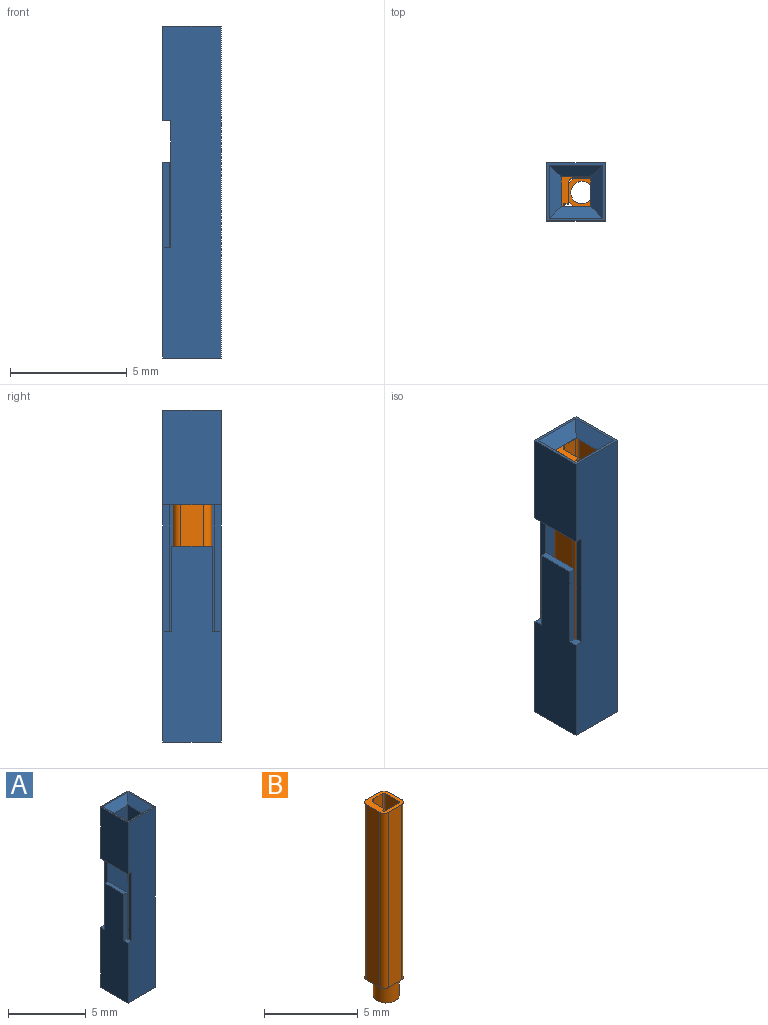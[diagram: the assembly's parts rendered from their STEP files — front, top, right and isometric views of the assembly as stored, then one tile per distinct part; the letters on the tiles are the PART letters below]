
ASSEMBLY  parts=2 mates=1
PART A: 25 faces, bbox 2.5x2.5x14.2 mm
  f0: plane 14.22x2.49mm, normal (0,-1,0), area 33.6mm2, adj f1,f2,f7,f12,f14,f20,f22,f23
  f1: plane 8.38x2.49mm, normal (-1,0,0), area 18.1mm2, adj f0,f7,f13,f17,f18,f19,f20,f21
  f2: plane 4.06x2.49mm, normal (-1,0,0), area 10.1mm2, adj f0,f13,f14,f22
  f3: plane 13.72x1.91mm, normal (0,1,0), area 25.9mm2, adj f4,f5,f7,f15,f16,f20,f22,f23
  f4: plane 8.38x1.91mm, normal (1,0,0), area 15.3mm2, adj f3,f6,f7,f17,f18,f19,f20,f21
  f5: plane 3.56x1.91mm, normal (1,0,0), area 6.8mm2, adj f3,f6,f16,f22
  f6: plane 13.72x1.91mm, normal (0,-1,0), area 25.9mm2, adj f4,f5,f7,f15,f16,f21,f22,f24
  f7: plane 2.49x2.49mm, normal (0,0,-1), area 2.6mm2, adj f0,f1,f3,f4,f6,f12,f13,f15
  f8: plane 2.29x0.51mm, normal (0,-0.71,0.71), area 1.3mm2, adj f9,f10,f14,f16
  f9: plane 2.29x0.51mm, normal (-0.71,0,0.71), area 1.3mm2, adj f8,f11,f14,f16
  f10: plane 2.29x0.51mm, normal (0.71,0,0.71), area 1.3mm2, adj f8,f11,f14,f16
  f11: plane 2.29x0.51mm, normal (0,0.71,0.71), area 1.3mm2, adj f9,f10,f14,f16
  f12: plane 14.22x2.49mm, normal (1,0,0), area 35.4mm2, adj f0,f7,f13,f14
  f13: plane 14.22x2.49mm, normal (0,1,0), area 33.6mm2, adj f1,f2,f7,f12,f14,f21,f22,f24
  f14: plane 2.49x2.49mm, normal (0,0,1), area 1mm2, adj f0,f2,f8,f9,f10,f11,f12,f13
  f15: plane 13.72x1.91mm, normal (-1,0,0), area 26.1mm2, adj f3,f6,f7,f16
  f16: plane 1.91x1.91mm, normal (0,0,-1), area 2mm2, adj f3,f5,f6,f8,f9,f10,f11,f15
  f17: plane 3.66x0.29mm, normal (0,1,0), area 1.1mm2, adj f1,f4,f18,f21
  f18: plane 1.73x0.29mm, normal (0,0,1), area 0.5mm2, adj f1,f4,f17,f19
  f19: plane 3.66x0.29mm, normal (0,-1,0), area 1.1mm2, adj f1,f4,f18,f20
  f20: plane 0.38x0.33mm, normal (0,0,1), area 0.1mm2, adj f0,f1,f3,f4,f19,f23
  f21: plane 0.38x0.33mm, normal (0,0,1), area 0.1mm2, adj f1,f4,f6,f13,f17,f24
  f22: plane 2.49x0.33mm, normal (0,0,-1), area 0.7mm2, adj f0,f2,f3,f5,f6,f13,f23,f24
  f23: plane 5.44x0.29mm, normal (-1,0,0), area 1.6mm2, adj f0,f3,f20,f22
  f24: plane 5.44x0.29mm, normal (-1,0,0), area 1.6mm2, adj f6,f13,f21,f22
PART B: 25 faces, bbox 1.7x1.7x12.7 mm
  f0: plane 0.31x0.03mm, normal (0,0,-1), area 0mm2, adj f1,f23
  f1: plane 11.43x0.99mm, normal (-1,0,0), area 11.3mm2, adj f0,f2,f17,f19,f21
  f2: cylinder r=0.13mm len=11.43mm, axis (0,0,1), area 2.3mm2, adj f1,f3,f18,f19,f21
  f3: plane 11.43x0.66mm, normal (0,-1,0), area 7.5mm2, adj f2,f4,f18,f19,f21
  f4: cylinder r=0.25mm len=11.43mm, axis (0,0,1), area 4.6mm2, adj f3,f5,f18,f19
  f5: plane 11.43x0.86mm, normal (1,0,0), area 9.8mm2, adj f4,f6,f18,f19,f21
  f6: plane 11.43x0.2mm, normal (0,-1,0), area 2.3mm2, adj f5,f7,f18,f19
  f7: cylinder r=0.13mm len=11.43mm, axis (0,0,1), area 2.3mm2, adj f6,f8,f18,f19
  f8: plane 11.43x0.99mm, normal (0,1,0), area 11.3mm2, adj f7,f17,f18,f19,f21
  f9: plane 11.43x0.99mm, normal (0,1,0), area 11.3mm2, adj f10,f16,f18,f19
  f10: cylinder r=0.33mm len=11.43mm, axis (0,0,1), area 5.9mm2, adj f9,f11,f18,f19
  f11: plane 11.43x0.99mm, normal (1,0,0), area 11.3mm2, adj f10,f12,f18,f19,f20
  f12: cylinder r=0.33mm len=11.43mm, axis (0,0,1), area 5.9mm2, adj f11,f13,f18,f19
  f13: plane 11.43x0.99mm, normal (0,-1,0), area 11.3mm2, adj f12,f14,f18,f19
  f14: cylinder r=0.33mm len=11.43mm, axis (0,0,1), area 5.9mm2, adj f13,f15,f18,f19
  f15: plane 11.43x0.99mm, normal (-1,0,0), area 11.3mm2, adj f14,f16,f18,f19
  f16: cylinder r=0.33mm len=11.43mm, axis (0,0,1), area 5.9mm2, adj f9,f15,f18,f19
  f17: cylinder r=0.13mm len=11.43mm, axis (0,0,1), area 2.3mm2, adj f1,f8,f18,f19,f21
  f18: plane 1.65x1.65mm, normal (0,0,-1), area 1.1mm2, adj f2,f3,f4,f5,f6,f7,f8,f9
  f19: plane 1.65x1.65mm, normal (0,0,1), area 1.3mm2, adj f1,f2,f3,f4,f5,f6,f7,f8
  f20: plane 0.37x0.03mm, normal (0,0,1), area 0mm2, adj f11,f22
  f21: plane 1.24x1.04mm, normal (0,0,1), area 0.5mm2, adj f1,f2,f3,f5,f8,f17,f22,f23
  f22: cylinder r=0.69mm len=1.37mm, axis (0,0,1), area 5.5mm2, adj f18,f20,f21,f24
  f23: cylinder r=0.48mm len=1.27mm, axis (0,0,1), area 3.9mm2, adj f0,f21,f24
  f24: plane 1.37x1.37mm, normal (0,0,-1), area 0.7mm2, adj f22,f23
PLACE A t=(-0.09,0.02,0)mm
PLACE B t=(4.66,0.32,0)mm
MATE fastened A.f16 <-> B.f19  axis (0,0,-1) through (-28.09,10.08,13.72)mm
